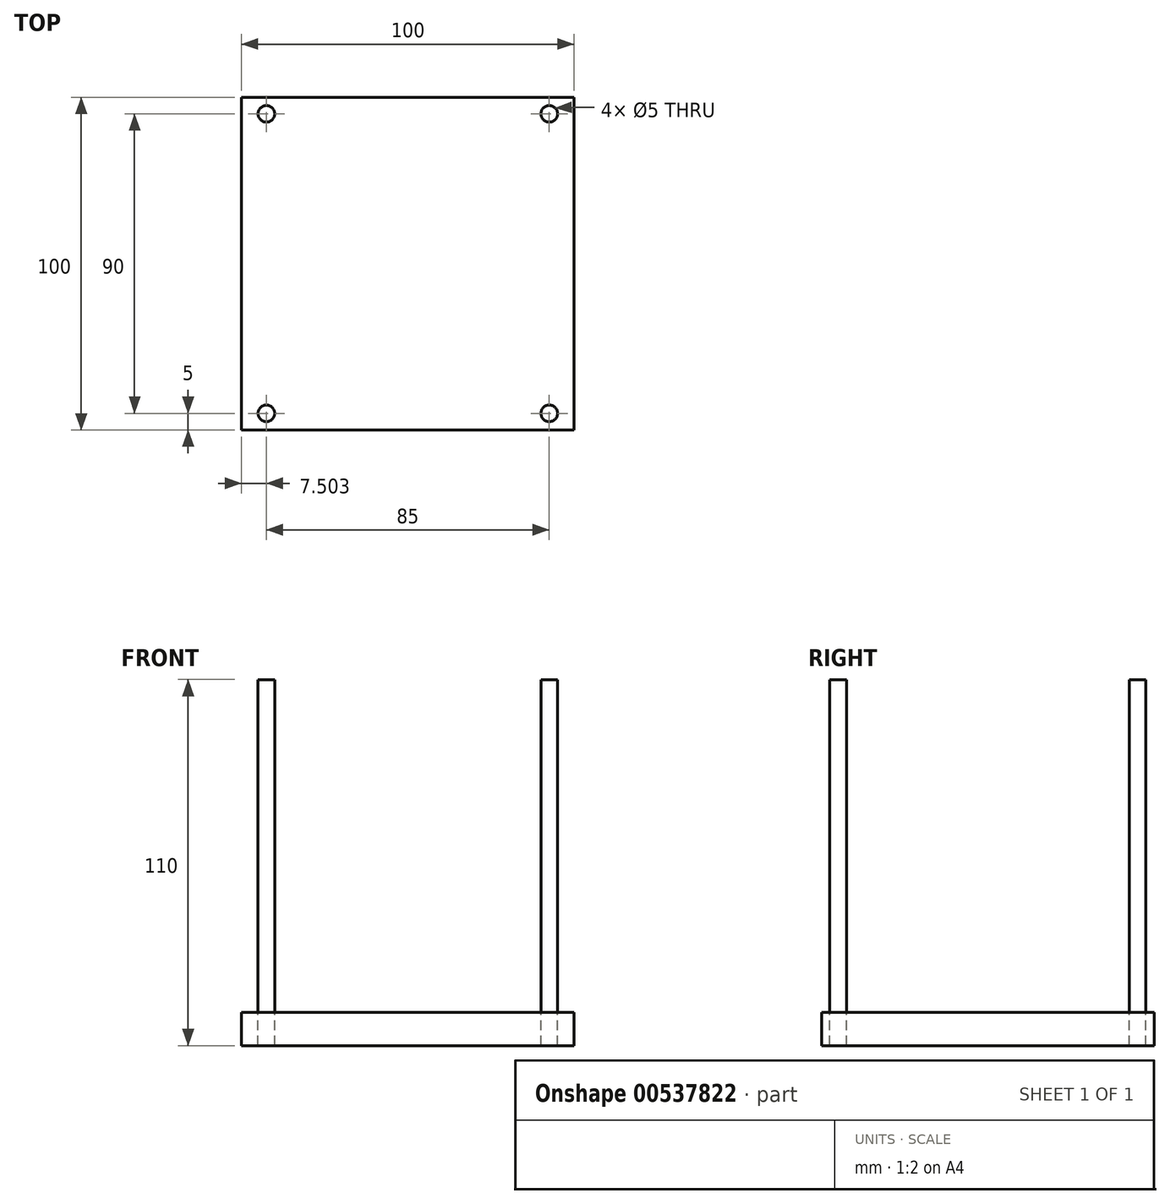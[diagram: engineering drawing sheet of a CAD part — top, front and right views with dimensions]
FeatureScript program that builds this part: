
annotation { "Feature Type Name" : "Feature", "Feature Type Description" : "" }
export const myFeature = defineFeature(function(context is Context, id is Id, definition is map)
    precondition{}
    {
        {
            var Q0;
            Q0=qCreatedBy(makeId("Front.planeOp"),FACE);
            var sketch = newSketch(context, id + "F0", { "sketchPlane" : qUnion([Q0])});
            skLineSegment(sketch, "E0.bottom", {"start": v(-75.84, 70.78) * mm, "end": v(24.16, 70.78) * mm});
            skLineSegment(sketch, "E0.top", {"start": v(-75.84, -29.22) * mm, "end": v(24.16, -29.22) * mm});
            skLineSegment(sketch, "E0.left", {"start": v(-75.84, 70.78) * mm, "end": v(-75.84, -29.22) * mm});
            skLineSegment(sketch, "E0.right", {"start": v(24.16, 70.78) * mm, "end": v(24.16, -29.22) * mm});
            skSolve(sketch);
        }
        {
            var Q0;
            Q0 = qSketchRegion(id + "F0", true);
            extrude(context, id + "F1", {"entities" : qUnion([Q0]), "depth" : 100 * mm, "offsetDistance" : 25 * mm});
        }
        {
            var Q0;
            Q0=makeQuery(id+"F1.opExtrude","SWEPT_FACE",FACE,{"disambiguationData":[OSD([sQuery(id+"F0.wireOp",EDGE,"E0.top")])]});
            var sketch = newSketch(context, id + "F2", { "sketchPlane" : qUnion([Q0])});
            skLineSegment(sketch, "E1.bottom", {"start": v(14.16, 10) * mm, "end": v(-65.84, 10) * mm});
            skLineSegment(sketch, "E1.top", {"start": v(14.16, 90) * mm, "end": v(-65.84, 90) * mm});
            skLineSegment(sketch, "E1.left", {"start": v(14.16, 10) * mm, "end": v(14.16, 90) * mm});
            skLineSegment(sketch, "E1.right", {"start": v(-65.84, 10) * mm, "end": v(-65.84, 90) * mm});
            skSolve(sketch);
        }
        {
            var Q0;
            Q0=makeQuery(id+"F2.imprint","IMPRINT",FACE,{"disambiguationData":[TD([[makeQuery(id+"F2.imprint","IMPRINT",EDGE,{"derivedFrom":sQuery(id+"F2.wireOp",EDGE,"E1.bottom")}),-1.0]])]});
            extrude(context, id + "F3", {"entities" : qUnion([Q0]), "operationType" : NewBodyOperationType.REMOVE, "endBound" : BoundingType.THROUGH_ALL, "oppositeDirection" : true, "depth" : 100 * mm, "offsetDistance" : 25 * mm});
        }
        {
            var Q0;
            Q0=makeQuery(id+"F1.opExtrude","SWEPT_FACE",FACE,{"disambiguationData":[OSD([sQuery(id+"F0.wireOp",EDGE,"E0.bottom")])]});
            var sketch = newSketch(context, id + "F4", { "sketchPlane" : qUnion([Q0])});
            skCircle(sketch, "E2", {"center": v(-68.34, -5) * mm, "radius": 2.5 * mm});
            skLineSegment(sketch, "E3", {"start": v(-25.84, 0) * mm, "end": v(-25.84, -100) * mm, "construction": true});
            skLineSegment(sketch, "E4", {"start": v(-75.84, -50) * mm, "end": v(24.16, -50) * mm, "construction": true});
            skCircle(sketch, "E5.MirrorC", {"center": v(16.66, -5) * mm, "radius": 2.5 * mm});
            skCircle(sketch, "E6.MirrorC", {"center": v(-68.34, -95) * mm, "radius": 2.5 * mm});
            skCircle(sketch, "E7.MirrorC", {"center": v(16.66, -95) * mm, "radius": 2.5 * mm});
            skSolve(sketch);
        }
        {
            var Q0;
            Q0=makeQuery(id+"F4.imprint","IMPRINT",FACE,{"disambiguationData":[TD([[makeQuery(id+"F4.imprint","IMPRINT",EDGE,{"derivedFrom":sQuery(id+"F4.wireOp",EDGE,"E6.MirrorC")}),-1.0]])]});
            var Q1;
            Q1=makeQuery(id+"F4.imprint","IMPRINT",FACE,{"disambiguationData":[TD([[makeQuery(id+"F4.imprint","IMPRINT",EDGE,{"derivedFrom":sQuery(id+"F4.wireOp",EDGE,"E2")}),1.0]])]});
            var Q2;
            Q2=makeQuery(id+"F4.imprint","IMPRINT",FACE,{"disambiguationData":[TD([[makeQuery(id+"F4.imprint","IMPRINT",EDGE,{"derivedFrom":sQuery(id+"F4.wireOp",EDGE,"E5.MirrorC")}),-1.0]])]});
            var Q3;
            Q3=makeQuery(id+"F4.imprint","IMPRINT",FACE,{"disambiguationData":[TD([[makeQuery(id+"F4.imprint","IMPRINT",EDGE,{"derivedFrom":sQuery(id+"F4.wireOp",EDGE,"E7.MirrorC")}),1.0]])]});
            extrude(context, id + "F5", {"entities" : qUnion([Q0, Q1, Q2, Q3]), "operationType" : NewBodyOperationType.REMOVE, "endBound" : BoundingType.THROUGH_ALL, "oppositeDirection" : true, "depth" : 25 * mm, "offsetDistance" : 25 * mm});
        }
        {
            var Q0;
            Q0=makeQuery(id+"F1.opExtrude","SWEPT_FACE",FACE,{"disambiguationData":[OSD([sQuery(id+"F0.wireOp",EDGE,"E0.top")])]});
            var sketch = newSketch(context, id + "F6", { "sketchPlane" : qUnion([Q0])});
            skCircle(sketch, "E8.0", {"center": v(-68.34, 95) * mm, "radius": 2.5 * mm});
            skLineSegment(sketch, "E9.0", {"start": v(-75.84, 100) * mm, "end": v(24.16, 100) * mm});
            skLineSegment(sketch, "E10.0", {"start": v(-75.84, 100) * mm, "end": v(-75.84, 0) * mm});
            skCircle(sketch, "E11.0", {"center": v(-68.34, 5) * mm, "radius": 2.5 * mm});
            skLineSegment(sketch, "E12.0", {"start": v(-75.84, 0) * mm, "end": v(24.16, 0) * mm});
            skCircle(sketch, "E13.0", {"center": v(16.66, 5) * mm, "radius": 2.5 * mm});
            skLineSegment(sketch, "E14.0", {"start": v(24.16, 100) * mm, "end": v(24.16, 0) * mm});
            skCircle(sketch, "E15.0", {"center": v(16.66, 95) * mm, "radius": 2.5 * mm});
            skSolve(sketch);
        }
        {
            var Q0;
            Q0 = qSketchRegion(id + "F6", true);
            extrude(context, id + "F7", {"entities" : qUnion([Q0]), "depth" : 10 * mm, "offsetDistance" : 25 * mm});
        }
    });
